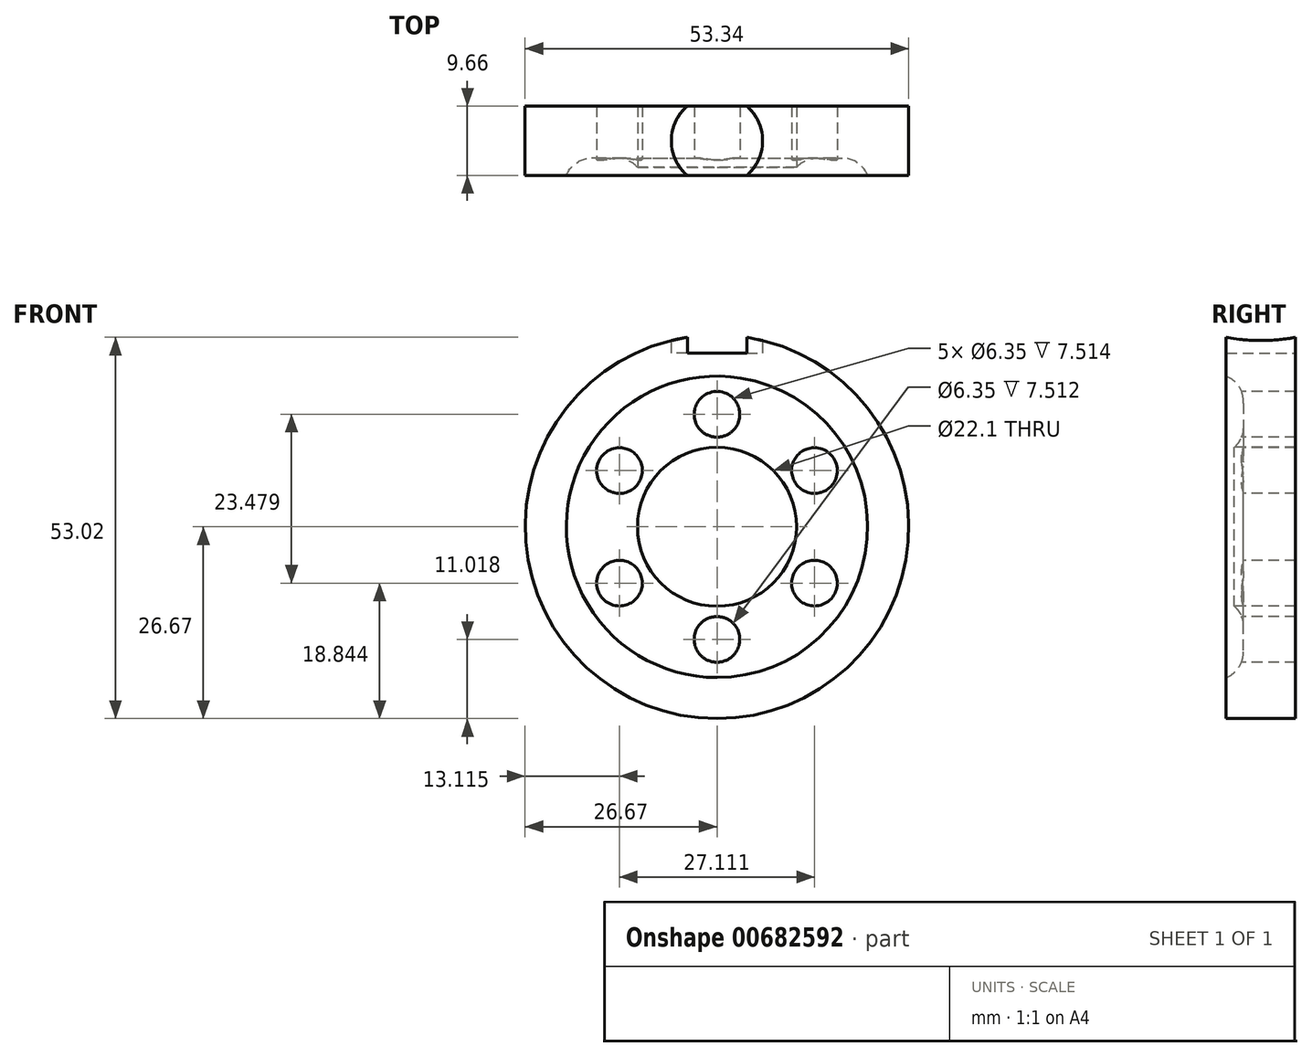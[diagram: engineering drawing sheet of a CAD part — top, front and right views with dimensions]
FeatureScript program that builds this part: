
annotation { "Feature Type Name" : "Feature", "Feature Type Description" : "" }
export const myFeature = defineFeature(function(context is Context, id is Id, definition is map)
    precondition{}
    {
        {
            var Q0;
            Q0=qCreatedBy(makeId("Front.planeOp"),FACE);
            var sketch = newSketch(context, id + "F0", { "sketchPlane" : qUnion([Q0])});
            skCircle(sketch, "E0", {"center": v(0, 0) * mm, "radius": 26.67 * mm});
            skSolve(sketch);
        }
        {
            var Q0;
            Q0=qSketchRegion(id+"F0",true);
            extrude(context, id + "F1", {"entities" : qUnion([Q0]), "endBound" : BoundingType.SYMMETRIC, "depth" : 9.65 * mm, "offsetDistance" : 25.4 * mm});
        }
        {
            var Q0;
            Q0=qCreatedBy(makeId("Top.planeOp"),FACE);
            cPlane(context, id + "F2", {"entities" : qUnion([Q0]), "cplaneType" : CPlaneType.OFFSET, "offset" : 27.94 * mm, "width" : 152.4 * mm, "height" : 152.4 * mm});
        }
        {
            var Q0;
            Q0=qCreatedBy(id+"F2.planeOp",FACE);
            var sketch = newSketch(context, id + "F3", { "sketchPlane" : qUnion([Q0])});
            skCircle(sketch, "E1", {"center": v(0, 0) * mm, "radius": 6.35 * mm});
            skArc(sketch, "E2", {"start": v(2.77, 0.64) * mm, "mid": v(4.48, 1.85) * mm, "end": v(5.7, 3.56) * mm, "construction": true});
            skArc(sketch, "E3", {"start": v(-2.77, -0.64) * mm, "mid": v(-4.48, -1.85) * mm, "end": v(-5.7, -3.56) * mm, "construction": true});
            skLineSegment(sketch, "E4", {"start": v(0, 6.35) * mm, "end": v(0, 0) * mm, "construction": true});
            skLineSegment(sketch, "E5", {"start": v(0, 0) * mm, "end": v(0, -6.35) * mm, "construction": true});
            skLineSegment(sketch, "E6", {"start": v(-2.77, 0.63) * mm, "end": v(-2.77, -0.64) * mm, "construction": true});
            skLineSegment(sketch, "E7", {"start": v(2.77, 0.63) * mm, "end": v(2.77, -0.64) * mm, "construction": true});
            skLineSegment(sketch, "E8", {"start": v(-5.7, 3.56) * mm, "end": v(-5.7, 4.83) * mm, "construction": true});
            skLineSegment(sketch, "E9", {"start": v(5.7, 3.56) * mm, "end": v(5.7, 4.83) * mm, "construction": true});
            skLineSegment(sketch, "E10.MirrorCS", {"start": v(-5.7, -3.56) * mm, "end": v(-5.7, -4.83) * mm, "construction": true});
            skLineSegment(sketch, "E11.MirrorCS", {"start": v(5.7, -3.56) * mm, "end": v(5.7, -4.83) * mm, "construction": true});
            skArc(sketch, "E12.trimOffspring", {"start": v(-5.7, 3.56) * mm, "mid": v(-4.48, 1.85) * mm, "end": v(-2.77, 0.64) * mm, "construction": true});
            skArc(sketch, "E13.trimOffspring", {"start": v(5.7, -3.56) * mm, "mid": v(4.48, -1.85) * mm, "end": v(2.77, -0.64) * mm, "construction": true});
            skLineSegment(sketch, "E14", {"start": v(5.7, 4.83) * mm, "end": v(-5.7, 4.83) * mm, "construction": true});
            skLineSegment(sketch, "E15", {"start": v(-5.7, -4.83) * mm, "end": v(5.7, -4.83) * mm, "construction": true});
            skSolve(sketch);
        }
        {
            var Q0;
            Q0=qSketchRegion(id+"F3",true);
            extrude(context, id + "F4", {"entities" : qUnion([Q0]), "operationType" : NewBodyOperationType.REMOVE, "oppositeDirection" : true, "depth" : 3.8 * mm, "offsetDistance" : 25.4 * mm});
        }
        {
            var Q0;
            Q0=makeQuery(id+"F1.opExtrude","CAP_FACE",FACE,{"disambiguationData":[OSD([sQuery(id+"F0.wireOp",EDGE,"E0")])],"isStart":false});
            var sketch = newSketch(context, id + "F5", { "sketchPlane" : qUnion([Q0])});
            skCircle(sketch, "E16", {"center": v(0, 0) * mm, "radius": 4 * mm});
            skSolve(sketch);
        }
        {
            var Q0;
            Q0=qSketchRegion(id+"F5",true);
            extrude(context, id + "F6", {"entities" : qUnion([Q0]), "operationType" : NewBodyOperationType.REMOVE, "oppositeDirection" : true, "depth" : 41.4 * mm, "offsetDistance" : 25.4 * mm});
        }
        {
            var Q0;
            Q0=makeQuery(id+"F1.opExtrude","CAP_FACE",FACE,{"disambiguationData":[OSD([sQuery(id+"F0.wireOp",EDGE,"E0")])],"isStart":false});
            var sketch = newSketch(context, id + "F7", { "sketchPlane" : qUnion([Q0])});
            skCircle(sketch, "E17", {"center": v(0, 0) * mm, "radius": 10.35 * mm});
            skCircle(sketch, "E18", {"center": v(0, 0) * mm, "radius": 20.96 * mm});
            skSolve(sketch);
        }
        {
            var Q0;
            Q0=qSketchRegion(id+"F7",true);
            extrude(context, id + "F8", {"entities" : qUnion([Q0]), "operationType" : NewBodyOperationType.REMOVE, "oppositeDirection" : true, "depth" : 2.41 * mm, "offsetDistance" : 25.4 * mm});
        }
        {
            var Q0;
            Q0=makeQuery(id+"F8.boolean.opBoolean","COPY",FACE,{"derivedFrom":makeQuery(id+"F8.opExtrude","CAP_FACE",FACE,{"disambiguationData":[OSD([sQuery(id+"F7.wireOp",EDGE,"E17"),sQuery(id+"F7.wireOp",EDGE,"E18")])],"isStart":false})});
            var sketch = newSketch(context, id + "F9", { "sketchPlane" : qUnion([Q0])});
            skCircle(sketch, "E19", {"center": v(0, 15.65) * mm, "radius": 3.18 * mm});
            skLineSegment(sketch, "E20", {"start": v(0, 15.65) * mm, "end": v(0, 20.96) * mm});
            skLineSegment(sketch, "E21", {"start": v(0, 15.65) * mm, "end": v(0, 10.35) * mm});
            skCircle(sketch, "E22.1.0", {"center": v(-13.56, 7.83) * mm, "radius": 3.18 * mm});
            skCircle(sketch, "E22.2.0", {"center": v(-13.56, -7.83) * mm, "radius": 3.18 * mm});
            skCircle(sketch, "E22.3.0", {"center": v(0, -15.65) * mm, "radius": 3.18 * mm});
            skCircle(sketch, "E22.4.0", {"center": v(13.56, -7.83) * mm, "radius": 3.18 * mm});
            skCircle(sketch, "E22.5.0", {"center": v(13.56, 7.83) * mm, "radius": 3.18 * mm});
            skPoint(sketch, "E22.center", {"position": v(0, 0) * mm});
            skSolve(sketch);
        }
        {
            var Q0;
            Q0=qSketchRegion(id+"F9",true);
            var Q1;
            Q1=qConstructionFilter(qBodyType(qCreatedBy(id+"F9",EDGE),BodyType.WIRE),ConstructionObject.NO);
            extrude(context, id + "F10", {"entities" : qUnion([Q0]), "operationType" : NewBodyOperationType.REMOVE, "surfaceEntities" : qUnion([Q1]), "oppositeDirection" : true, "depth" : 25.4 * mm, "offsetDistance" : 25.4 * mm});
        }
        {
            var Q0;
            Q0=makeQuery(id+"F8.boolean.opBoolean","COPY",EDGE,{"derivedFrom":makeQuery(id+"F8.opExtrude","CAP_EDGE",EDGE,{"disambiguationData":[OSD([sQuery(id+"F7.wireOp",EDGE,"E18")])],"isStart":false})});
            var Q1;
            Q1=makeQuery(id+"F8.boolean.opBoolean","COPY",EDGE,{"derivedFrom":makeQuery(id+"F8.opExtrude","CAP_EDGE",EDGE,{"disambiguationData":[OSD([sQuery(id+"F7.wireOp",EDGE,"E17")])],"isStart":false})});
            var Q2;
            Q2=makeQuery(id+"FceMFZ39dj65BmD_1.1.F8.boolean.opBoolean","COPY",EDGE,{"derivedFrom":makeQuery(id+"FceMFZ39dj65BmD_1.1.F8.opExtrude","CAP_EDGE",EDGE,{"disambiguationData":[OSD([sQuery(id+"F7.wireOp",EDGE,"E18")])],"isStart":false})});
            var Q3;
            Q3=makeQuery(id+"FceMFZ39dj65BmD_1.1.F8.boolean.opBoolean","COPY",EDGE,{"derivedFrom":makeQuery(id+"FceMFZ39dj65BmD_1.1.F8.opExtrude","CAP_EDGE",EDGE,{"disambiguationData":[OSD([sQuery(id+"F7.wireOp",EDGE,"E17")])],"isStart":false})});
            fillet(context, id + "F11", {"entities" : qUnion([Q0, Q1, Q2, Q3]), "radius" : 3.8 * mm, "tangentPropagation" : true, "allowEdgeOverflow" : false});
        }
        {
            var Q0;
            Q0=makeQuery(id+"F8.boolean.opBoolean","SPLIT",FACE,{"disambiguationData":[TD([makeQuery(id+"F6.boolean.opBoolean","COPY",FACE,{"derivedFrom":makeQuery(id+"F6.opExtrude","SWEPT_FACE",FACE,{"disambiguationData":[OSD([sQuery(id+"F5.wireOp",EDGE,"E16")])]})})])],"derivedFrom":makeQuery(id+"F1.opExtrude","CAP_FACE",FACE,{"disambiguationData":[OSD([sQuery(id+"F0.wireOp",EDGE,"E0")])],"isStart":false})});
            var sketch = newSketch(context, id + "F12", { "sketchPlane" : qUnion([Q0])});
            skCircle(sketch, "E23", {"center": v(0, 0) * mm, "radius": 11.05 * mm});
            skSolve(sketch);
        }
        {
            var Q0;
            Q0 = qSketchRegion(id + "F12", true);
            extrude(context, id + "F13", {"entities" : qUnion([Q0]), "operationType" : NewBodyOperationType.REMOVE, "oppositeDirection" : true, "depth" : 25.4 * mm, "offsetDistance" : 25.4 * mm});
        }
    });
